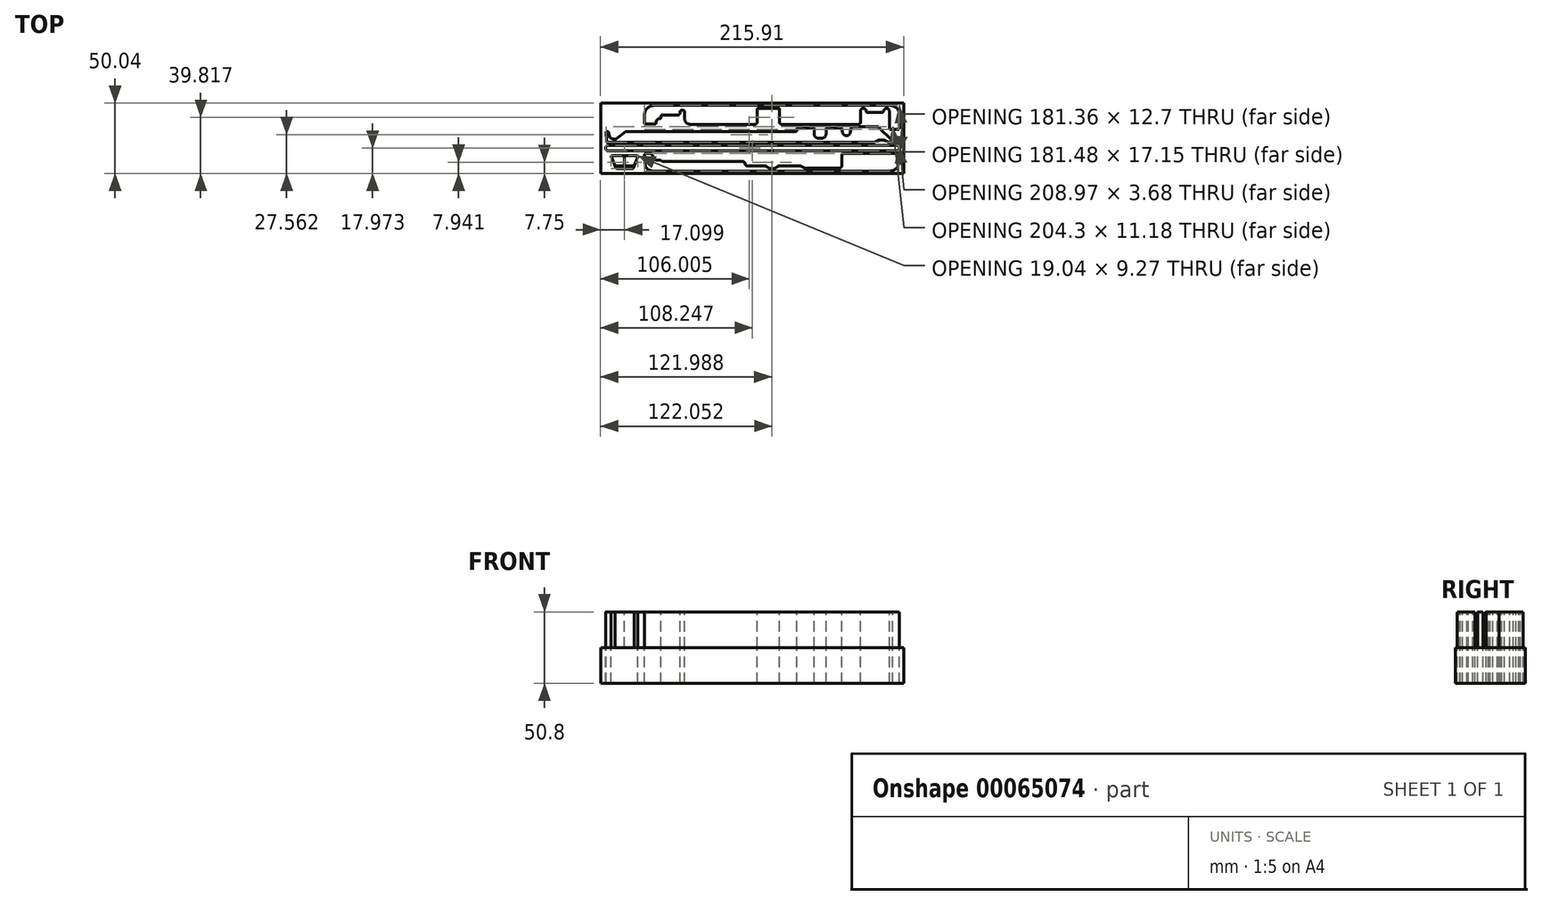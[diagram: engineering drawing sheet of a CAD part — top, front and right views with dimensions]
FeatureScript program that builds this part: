
annotation { "Feature Type Name" : "Feature", "Feature Type Description" : "" }
export const myFeature = defineFeature(function(context is Context, id is Id, definition is map)
    precondition{}
    {
        {
            var Q0;
            Q0=qCreatedBy(makeId("Top.planeOp"),FACE);
            var sketch = newSketch(context, id + "F0", { "sketchPlane" : qUnion([Q0])});
            skLineSegment(sketch, "E0", {"start": v(-180.88, 0) * mm, "end": v(0, 0) * mm});
            skLineSegment(sketch, "E1", {"start": v(0, 0) * mm, "end": v(0, 11.43) * mm});
            skLineSegment(sketch, "E2", {"start": v(-1.27, 12.7) * mm, "end": v(-39.67, 12.7) * mm});
            skLineSegment(sketch, "E3", {"start": v(-40.94, 11.43) * mm, "end": v(-40.94, 3.63) * mm});
            skLineSegment(sketch, "E4", {"start": v(-42.21, 2.36) * mm, "end": v(-67.28, 2.36) * mm});
            skLineSegment(sketch, "E5", {"start": v(-67.82, 2.48) * mm, "end": v(-70.48, 3.74) * mm});
            skLineSegment(sketch, "E6", {"start": v(-71.02, 3.86) * mm, "end": v(-85.51, 3.86) * mm});
            skLineSegment(sketch, "E7", {"start": v(-86.15, 3.7) * mm, "end": v(-88.59, 2.29) * mm});
            skLineSegment(sketch, "E8", {"start": v(-92.39, 2.29) * mm, "end": v(-94.83, 3.7) * mm});
            skLineSegment(sketch, "E9", {"start": v(-95.46, 3.86) * mm, "end": v(-108.29, 3.86) * mm});
            skLineSegment(sketch, "E10", {"start": v(-109.47, 4.65) * mm, "end": v(-110.1, 6.2) * mm});
            skLineSegment(sketch, "E11", {"start": v(-111.27, 6.98) * mm, "end": v(-168.18, 6.98) * mm});
            skLineSegment(sketch, "E12", {"start": v(-168.8, 7.15) * mm, "end": v(-170.13, 7.9) * mm});
            skLineSegment(sketch, "E13", {"start": v(-170.76, 8.08) * mm, "end": v(-173.2, 8.08) * mm});
            skLineSegment(sketch, "E14", {"start": v(-174.38, 8.9) * mm, "end": v(-174.9, 10.28) * mm});
            skLineSegment(sketch, "E15", {"start": v(-175.06, 10.53) * mm, "end": v(-176.6, 12.38) * mm});
            skLineSegment(sketch, "E16", {"start": v(-177.28, 12.7) * mm, "end": v(-180.47, 12.7) * mm});
            skLineSegment(sketch, "E17", {"start": v(-181.36, 11.78) * mm, "end": v(-180.88, 0) * mm});
            skFitSpline(sketch, "E18", {"points": [v(-181.13, 6.1) * mm, v(-172.76, 0) * mm], "startDerivative": vector(0.46, -11.6) * mm, "endDerivative": vector(18.6, 0) * mm});
            skFitSpline(sketch, "E19", {"points": [v(0, 6.73) * mm, v(-7.37, 0) * mm], "startDerivative": vector(0, -6.53) * mm, "endDerivative": vector(-15.85, 0) * mm});
            skPoint(sketch, "E20.visualSharp", {"position": v(0, 12.7) * mm});
            skArc(sketch, "E20.filletArc", {"start": v(0, 11.43) * mm, "mid": v(-0.37, 12.33) * mm, "end": v(-1.27, 12.7) * mm});
            skPoint(sketch, "E21.visualSharp", {"position": v(-40.94, 12.7) * mm});
            skArc(sketch, "E21.filletArc", {"start": v(-39.67, 12.7) * mm, "mid": v(-40.57, 12.33) * mm, "end": v(-40.94, 11.43) * mm});
            skPoint(sketch, "E22.visualSharp", {"position": v(-40.94, 2.36) * mm});
            skArc(sketch, "E22.filletArc", {"start": v(-42.21, 2.36) * mm, "mid": v(-41.32, 2.73) * mm, "end": v(-40.94, 3.63) * mm});
            skPoint(sketch, "E23.visualSharp", {"position": v(-67.56, 2.36) * mm});
            skArc(sketch, "E23.filletArc", {"start": v(-67.82, 2.48) * mm, "mid": v(-67.56, 2.4) * mm, "end": v(-67.28, 2.36) * mm});
            skPoint(sketch, "E24.visualSharp", {"position": v(-70.74, 3.86) * mm});
            skArc(sketch, "E24.filletArc", {"start": v(-70.48, 3.74) * mm, "mid": v(-70.75, 3.83) * mm, "end": v(-71.02, 3.86) * mm});
            skPoint(sketch, "E25.visualSharp", {"position": v(-85.85, 3.86) * mm});
            skArc(sketch, "E25.filletArc", {"start": v(-85.51, 3.86) * mm, "mid": v(-85.84, 3.82) * mm, "end": v(-86.15, 3.7) * mm});
            skPoint(sketch, "E26.visualSharp", {"position": v(-95.12, 3.86) * mm});
            skArc(sketch, "E26.filletArc", {"start": v(-94.83, 3.7) * mm, "mid": v(-95.13, 3.82) * mm, "end": v(-95.46, 3.86) * mm});
            skPoint(sketch, "E27.visualSharp", {"position": v(-109.14, 3.86) * mm});
            skArc(sketch, "E27.filletArc", {"start": v(-109.47, 4.65) * mm, "mid": v(-109, 4.08) * mm, "end": v(-108.29, 3.86) * mm});
            skPoint(sketch, "E28.visualSharp", {"position": v(-110.41, 6.98) * mm});
            skArc(sketch, "E28.filletArc", {"start": v(-110.1, 6.2) * mm, "mid": v(-110.56, 6.77) * mm, "end": v(-111.27, 6.99) * mm});
            skPoint(sketch, "E29.visualSharp", {"position": v(-168.51, 6.98) * mm});
            skArc(sketch, "E29.filletArc", {"start": v(-168.8, 7.15) * mm, "mid": v(-168.5, 7.03) * mm, "end": v(-168.18, 6.98) * mm});
            skPoint(sketch, "E30.visualSharp", {"position": v(-170.42, 8.08) * mm});
            skArc(sketch, "E30.filletArc", {"start": v(-170.13, 7.9) * mm, "mid": v(-170.43, 8.03) * mm, "end": v(-170.76, 8.08) * mm});
            skPoint(sketch, "E31.visualSharp", {"position": v(-174.07, 8.08) * mm});
            skArc(sketch, "E31.filletArc", {"start": v(-174.38, 8.9) * mm, "mid": v(-173.92, 8.3) * mm, "end": v(-173.2, 8.08) * mm});
            skPoint(sketch, "E32.visualSharp", {"position": v(-181.4, 12.7) * mm});
            skArc(sketch, "E32.filletArc", {"start": v(-180.47, 12.7) * mm, "mid": v(-181.1, 12.43) * mm, "end": v(-181.36, 11.78) * mm});
            skPoint(sketch, "E33.visualSharp", {"position": v(-176.87, 12.7) * mm});
            skArc(sketch, "E33.filletArc", {"start": v(-176.6, 12.38) * mm, "mid": v(-176.9, 12.62) * mm, "end": v(-177.28, 12.7) * mm});
            skPoint(sketch, "E34.visualSharp", {"position": v(-174.96, 10.41) * mm});
            skArc(sketch, "E34.filletArc", {"start": v(-174.9, 10.28) * mm, "mid": v(-174.97, 10.4) * mm, "end": v(-175.06, 10.53) * mm});
            skPoint(sketch, "E35.visualSharp", {"position": v(-90.49, 1.2) * mm});
            skArc(sketch, "E35.filletArc", {"start": v(-92.39, 2.29) * mm, "mid": v(-90.49, 1.78) * mm, "end": v(-88.59, 2.29) * mm});
            skLineSegment(sketch, "E36.bottom", {"start": v(-207.7, 18.41) * mm, "end": v(-1.27, 18.41) * mm});
            skLineSegment(sketch, "E36.top", {"start": v(-207.7, 14.73) * mm, "end": v(-1.27, 14.73) * mm});
            skLineSegment(sketch, "E36.left", {"start": v(-208.97, 17.14) * mm, "end": v(-208.97, 16) * mm});
            skLineSegment(sketch, "E36.right", {"start": v(0, 17.14) * mm, "end": v(0, 16) * mm});
            skPoint(sketch, "E37.visualSharp", {"position": v(-208.97, 18.41) * mm});
            skArc(sketch, "E37.filletArc", {"start": v(-207.7, 18.41) * mm, "mid": v(-208.6, 18.04) * mm, "end": v(-208.97, 17.14) * mm});
            skPoint(sketch, "E38.visualSharp", {"position": v(-208.97, 14.73) * mm});
            skArc(sketch, "E38.filletArc", {"start": v(-208.97, 16) * mm, "mid": v(-208.6, 15.1) * mm, "end": v(-207.7, 14.73) * mm});
            skPoint(sketch, "E39.visualSharp", {"position": v(0, 18.41) * mm});
            skArc(sketch, "E39.filletArc", {"start": v(0, 17.14) * mm, "mid": v(-0.37, 18.04) * mm, "end": v(-1.27, 18.41) * mm});
            skPoint(sketch, "E40.visualSharp", {"position": v(0, 14.73) * mm});
            skArc(sketch, "E40.filletArc", {"start": v(-1.27, 14.73) * mm, "mid": v(-0.37, 15.1) * mm, "end": v(0, 16) * mm});
            skLineSegment(sketch, "E41", {"start": v(-204.4, 11.18) * mm, "end": v(-186.87, 11.18) * mm});
            skLineSegment(sketch, "E42", {"start": v(-186.17, 10.12) * mm, "end": v(-189.46, 2.37) * mm});
            skLineSegment(sketch, "E43", {"start": v(-190.17, 1.9) * mm, "end": v(-201.1, 1.9) * mm});
            skLineSegment(sketch, "E44", {"start": v(-201.8, 2.37) * mm, "end": v(-205.1, 10.12) * mm});
            skPoint(sketch, "E45.visualSharp", {"position": v(-205.55, 11.18) * mm});
            skArc(sketch, "E45.filletArc", {"start": v(-204.4, 11.18) * mm, "mid": v(-205.03, 10.83) * mm, "end": v(-205.1, 10.12) * mm});
            skPoint(sketch, "E46.visualSharp", {"position": v(-185.72, 11.18) * mm});
            skArc(sketch, "E46.filletArc", {"start": v(-186.17, 10.12) * mm, "mid": v(-186.23, 10.83) * mm, "end": v(-186.87, 11.18) * mm});
            skPoint(sketch, "E47.visualSharp", {"position": v(-189.66, 1.9) * mm});
            skArc(sketch, "E47.filletArc", {"start": v(-190.17, 1.9) * mm, "mid": v(-189.75, 2.03) * mm, "end": v(-189.46, 2.37) * mm});
            skPoint(sketch, "E48.visualSharp", {"position": v(-201.6, 1.9) * mm});
            skArc(sketch, "E48.filletArc", {"start": v(-201.8, 2.37) * mm, "mid": v(-201.52, 2.03) * mm, "end": v(-201.1, 1.9) * mm});
            skLineSegment(sketch, "E49", {"start": v(-202.46, 3.94) * mm, "end": v(-188.8, 3.94) * mm});
            skLineSegment(sketch, "E50", {"start": v(-195.63, 3.94) * mm, "end": v(-195.63, 11.18) * mm});
            skLineSegment(sketch, "E51", {"start": v(-207.8, 20.57) * mm, "end": v(-17.9, 20.57) * mm});
            skArc(sketch, "E52", {"start": v(-7.43, 20.72) * mm, "mid": v(-12.45, 22.35) * mm, "end": v(-17.46, 20.72) * mm});
            skLineSegment(sketch, "E53", {"start": v(-6.98, 20.57) * mm, "end": v(-5.33, 20.57) * mm});
            skLineSegment(sketch, "E54", {"start": v(-4.8, 21.88) * mm, "end": v(-14.64, 31.53) * mm});
            skLineSegment(sketch, "E55", {"start": v(-15.17, 31.75) * mm, "end": v(-33.5, 31.75) * mm});
            skLineSegment(sketch, "E56", {"start": v(-34.25, 31.09) * mm, "end": v(-34.66, 27.91) * mm});
            skArc(sketch, "E57", {"start": v(-40.37, 27.91) * mm, "mid": v(-37.51, 25.4) * mm, "end": v(-34.66, 27.91) * mm});
            skLineSegment(sketch, "E58", {"start": v(-40.37, 27.91) * mm, "end": v(-40.68, 30.32) * mm});
            skLineSegment(sketch, "E59", {"start": v(-41.44, 30.99) * mm, "end": v(-51.3, 30.99) * mm});
            skLineSegment(sketch, "E60", {"start": v(-52.07, 30.23) * mm, "end": v(-52.07, 26.42) * mm});
            skLineSegment(sketch, "E61", {"start": v(-54.86, 23.62) * mm, "end": v(-57.66, 23.62) * mm});
            skLineSegment(sketch, "E62", {"start": v(-60.45, 26.42) * mm, "end": v(-60.45, 30.23) * mm});
            skLineSegment(sketch, "E63", {"start": v(-61.21, 30.99) * mm, "end": v(-72, 30.99) * mm});
            skLineSegment(sketch, "E64", {"start": v(-72.77, 30.23) * mm, "end": v(-72.77, 29.21) * mm});
            skLineSegment(sketch, "E65", {"start": v(-73.53, 28.45) * mm, "end": v(-194.3, 28.45) * mm});
            skLineSegment(sketch, "E66", {"start": v(-194.77, 28.29) * mm, "end": v(-201.34, 23.15) * mm});
            skLineSegment(sketch, "E67", {"start": v(-201.81, 22.99) * mm, "end": v(-203.32, 22.99) * mm});
            skLineSegment(sketch, "E68", {"start": v(-203.58, 23.03) * mm, "end": v(-205.86, 23.86) * mm});
            skLineSegment(sketch, "E69", {"start": v(-206.34, 24.4) * mm, "end": v(-207.13, 27.86) * mm});
            skLineSegment(sketch, "E70", {"start": v(-207.87, 28.45) * mm, "end": v(-208.11, 28.45) * mm});
            skLineSegment(sketch, "E71", {"start": v(-208.87, 27.65) * mm, "end": v(-208.57, 21.3) * mm});
            skPoint(sketch, "E72.visualSharp", {"position": v(-3.47, 20.57) * mm});
            skArc(sketch, "E72.filletArc", {"start": v(-5.33, 20.57) * mm, "mid": v(-4.63, 21.05) * mm, "end": v(-4.8, 21.88) * mm});
            skPoint(sketch, "E73.visualSharp", {"position": v(-14.86, 31.75) * mm});
            skArc(sketch, "E73.filletArc", {"start": v(-14.64, 31.53) * mm, "mid": v(-14.88, 31.7) * mm, "end": v(-15.17, 31.75) * mm});
            skPoint(sketch, "E74.visualSharp", {"position": v(-34.16, 31.75) * mm});
            skArc(sketch, "E74.filletArc", {"start": v(-33.5, 31.75) * mm, "mid": v(-34, 31.56) * mm, "end": v(-34.25, 31.09) * mm});
            skPoint(sketch, "E75.visualSharp", {"position": v(-40.77, 30.99) * mm});
            skArc(sketch, "E75.filletArc", {"start": v(-40.68, 30.32) * mm, "mid": v(-40.93, 30.8) * mm, "end": v(-41.44, 30.99) * mm});
            skPoint(sketch, "E76.visualSharp", {"position": v(-52.07, 30.99) * mm});
            skArc(sketch, "E76.filletArc", {"start": v(-51.3, 30.99) * mm, "mid": v(-51.85, 30.76) * mm, "end": v(-52.07, 30.23) * mm});
            skPoint(sketch, "E77.visualSharp", {"position": v(-60.45, 30.99) * mm});
            skArc(sketch, "E77.filletArc", {"start": v(-60.45, 30.23) * mm, "mid": v(-60.68, 30.76) * mm, "end": v(-61.21, 30.99) * mm});
            skPoint(sketch, "E78.visualSharp", {"position": v(-72.77, 30.99) * mm});
            skArc(sketch, "E78.filletArc", {"start": v(-72, 30.99) * mm, "mid": v(-72.55, 30.76) * mm, "end": v(-72.77, 30.23) * mm});
            skPoint(sketch, "E79.visualSharp", {"position": v(-72.77, 28.45) * mm});
            skArc(sketch, "E79.filletArc", {"start": v(-73.53, 28.45) * mm, "mid": v(-73, 28.67) * mm, "end": v(-72.77, 29.21) * mm});
            skPoint(sketch, "E80.visualSharp", {"position": v(-194.56, 28.45) * mm});
            skArc(sketch, "E80.filletArc", {"start": v(-194.3, 28.45) * mm, "mid": v(-194.55, 28.4) * mm, "end": v(-194.77, 28.29) * mm});
            skPoint(sketch, "E81.visualSharp", {"position": v(-201.55, 22.99) * mm});
            skArc(sketch, "E81.filletArc", {"start": v(-201.81, 22.99) * mm, "mid": v(-201.56, 23.03) * mm, "end": v(-201.34, 23.15) * mm});
            skPoint(sketch, "E82.visualSharp", {"position": v(-203.45, 22.99) * mm});
            skArc(sketch, "E82.filletArc", {"start": v(-203.58, 23.03) * mm, "mid": v(-203.45, 23) * mm, "end": v(-203.32, 22.99) * mm});
            skPoint(sketch, "E83.visualSharp", {"position": v(-206.25, 24) * mm});
            skArc(sketch, "E83.filletArc", {"start": v(-206.34, 24.4) * mm, "mid": v(-206.17, 24.07) * mm, "end": v(-205.86, 23.86) * mm});
            skPoint(sketch, "E84.visualSharp", {"position": v(-207.26, 28.45) * mm});
            skArc(sketch, "E84.filletArc", {"start": v(-207.13, 27.86) * mm, "mid": v(-207.4, 28.28) * mm, "end": v(-207.87, 28.45) * mm});
            skPoint(sketch, "E85.visualSharp", {"position": v(-208.91, 28.45) * mm});
            skArc(sketch, "E85.filletArc", {"start": v(-208.11, 28.45) * mm, "mid": v(-208.67, 28.21) * mm, "end": v(-208.87, 27.65) * mm});
            skPoint(sketch, "E86.visualSharp", {"position": v(-208.53, 20.57) * mm});
            skArc(sketch, "E86.filletArc", {"start": v(-208.57, 21.3) * mm, "mid": v(-208.33, 20.78) * mm, "end": v(-207.8, 20.57) * mm});
            skPoint(sketch, "E87.visualSharp", {"position": v(-52.07, 23.62) * mm});
            skArc(sketch, "E87.filletArc", {"start": v(-54.86, 23.62) * mm, "mid": v(-52.89, 24.44) * mm, "end": v(-52.07, 26.42) * mm});
            skPoint(sketch, "E88.visualSharp", {"position": v(-60.45, 23.62) * mm});
            skArc(sketch, "E88.filletArc", {"start": v(-60.45, 26.42) * mm, "mid": v(-59.63, 24.44) * mm, "end": v(-57.66, 23.62) * mm});
            skLineSegment(sketch, "E89", {"start": v(-14.86, 31.75) * mm, "end": v(-4.57, 31.75) * mm, "construction": true});
            skLineSegment(sketch, "E90", {"start": v(-4.57, 31.75) * mm, "end": v(-4.57, 21.34) * mm, "construction": true});
            skPoint(sketch, "E91.visualSharp", {"position": v(-17.65, 20.57) * mm});
            skArc(sketch, "E91.filletArc", {"start": v(-17.9, 20.57) * mm, "mid": v(-17.67, 20.61) * mm, "end": v(-17.46, 20.72) * mm});
            skPoint(sketch, "E92.visualSharp", {"position": v(-7.24, 20.57) * mm});
            skArc(sketch, "E92.filletArc", {"start": v(-7.43, 20.72) * mm, "mid": v(-7.22, 20.61) * mm, "end": v(-6.98, 20.57) * mm});
            skLineSegment(sketch, "E93", {"start": v(-181.48, 47) * mm, "end": v(-181.48, 34.42) * mm});
            skLineSegment(sketch, "E94", {"start": v(-180.72, 33.66) * mm, "end": v(-173.92, 33.66) * mm});
            skLineSegment(sketch, "E95", {"start": v(-173.16, 34.34) * mm, "end": v(-173.07, 35.3) * mm});
            skLineSegment(sketch, "E96", {"start": v(-170.54, 37.6) * mm, "end": v(-170.43, 37.6) * mm});
            skLineSegment(sketch, "E97", {"start": v(-169.67, 38.35) * mm, "end": v(-169.67, 39.37) * mm});
            skLineSegment(sketch, "E98", {"start": v(-168.9, 40.13) * mm, "end": v(-157.6, 40.13) * mm});
            skLineSegment(sketch, "E99", {"start": v(-156.08, 41.66) * mm, "end": v(-156.08, 42.16) * mm});
            skLineSegment(sketch, "E100", {"start": v(-154.56, 43.69) * mm, "end": v(-154.3, 43.69) * mm});
            skLineSegment(sketch, "E101", {"start": v(-152.78, 42.16) * mm, "end": v(-152.78, 37.34) * mm});
            skLineSegment(sketch, "E102", {"start": v(-148.97, 33.53) * mm, "end": v(-102.62, 33.53) * mm});
            skLineSegment(sketch, "E103", {"start": v(-101.1, 35.05) * mm, "end": v(-101.1, 44.2) * mm});
            skLineSegment(sketch, "E104", {"start": v(-100.33, 44.96) * mm, "end": v(-85.98, 44.96) * mm});
            skLineSegment(sketch, "E105", {"start": v(-85.22, 44.2) * mm, "end": v(-85.22, 35.05) * mm});
            skLineSegment(sketch, "E106", {"start": v(-83.7, 33.53) * mm, "end": v(-28.96, 33.53) * mm});
            skLineSegment(sketch, "E107", {"start": v(-27.43, 35.05) * mm, "end": v(-27.43, 43.05) * mm});
            skArc(sketch, "E108", {"start": v(-23.76, 43.78) * mm, "mid": v(-25.9, 44.92) * mm, "end": v(-27.43, 43.05) * mm});
            skLineSegment(sketch, "E109", {"start": v(-23.76, 43.78) * mm, "end": v(-23.24, 42.5) * mm});
            skLineSegment(sketch, "E110", {"start": v(-22.54, 42.04) * mm, "end": v(-11.88, 42.04) * mm});
            skLineSegment(sketch, "E111", {"start": v(-11.17, 42.5) * mm, "end": v(-10.65, 43.78) * mm});
            skArc(sketch, "E112", {"start": v(-6.98, 43.05) * mm, "mid": v(-8.52, 44.92) * mm, "end": v(-10.65, 43.78) * mm});
            skLineSegment(sketch, "E113", {"start": v(-6.98, 43.05) * mm, "end": v(-6.98, 30.6) * mm});
            skLineSegment(sketch, "E114", {"start": v(-6.22, 29.84) * mm, "end": v(-0.76, 29.84) * mm});
            skLineSegment(sketch, "E115", {"start": v(0, 30.6) * mm, "end": v(0, 47) * mm});
            skLineSegment(sketch, "E116", {"start": v(0, 47) * mm, "end": v(-181.48, 47) * mm});
            skPoint(sketch, "E117.visualSharp", {"position": v(-23.05, 42.04) * mm});
            skArc(sketch, "E117.filletArc", {"start": v(-23.24, 42.5) * mm, "mid": v(-22.96, 42.17) * mm, "end": v(-22.54, 42.04) * mm});
            skPoint(sketch, "E118.visualSharp", {"position": v(-11.37, 42.04) * mm});
            skArc(sketch, "E118.filletArc", {"start": v(-11.88, 42.04) * mm, "mid": v(-11.45, 42.17) * mm, "end": v(-11.17, 42.5) * mm});
            skPoint(sketch, "E119.visualSharp", {"position": v(-6.98, 29.84) * mm});
            skArc(sketch, "E119.filletArc", {"start": v(-6.98, 30.6) * mm, "mid": v(-6.76, 30.07) * mm, "end": v(-6.22, 29.84) * mm});
            skPoint(sketch, "E120.visualSharp", {"position": v(0, 29.84) * mm});
            skArc(sketch, "E120.filletArc", {"start": v(-0.76, 29.84) * mm, "mid": v(-0.22, 30.07) * mm, "end": v(0, 30.6) * mm});
            skPoint(sketch, "E121.visualSharp", {"position": v(-101.1, 44.96) * mm});
            skArc(sketch, "E121.filletArc", {"start": v(-100.33, 44.96) * mm, "mid": v(-100.87, 44.73) * mm, "end": v(-101.1, 44.2) * mm});
            skPoint(sketch, "E122.visualSharp", {"position": v(-85.22, 44.96) * mm});
            skArc(sketch, "E122.filletArc", {"start": v(-85.22, 44.2) * mm, "mid": v(-85.44, 44.73) * mm, "end": v(-85.98, 44.96) * mm});
            skPoint(sketch, "E123.visualSharp", {"position": v(-169.67, 37.6) * mm});
            skArc(sketch, "E123.filletArc", {"start": v(-170.43, 37.6) * mm, "mid": v(-169.9, 37.82) * mm, "end": v(-169.67, 38.35) * mm});
            skPoint(sketch, "E124.visualSharp", {"position": v(-169.67, 40.13) * mm});
            skArc(sketch, "E124.filletArc", {"start": v(-168.9, 40.13) * mm, "mid": v(-169.45, 39.9) * mm, "end": v(-169.67, 39.37) * mm});
            skPoint(sketch, "E125.visualSharp", {"position": v(-181.48, 33.66) * mm});
            skArc(sketch, "E125.filletArc", {"start": v(-181.48, 34.42) * mm, "mid": v(-181.26, 33.88) * mm, "end": v(-180.72, 33.66) * mm});
            skPoint(sketch, "E126.visualSharp", {"position": v(-173.23, 33.66) * mm});
            skArc(sketch, "E126.filletArc", {"start": v(-173.92, 33.65) * mm, "mid": v(-173.4, 33.85) * mm, "end": v(-173.16, 34.34) * mm});
            skPoint(sketch, "E127.visualSharp", {"position": v(-101.1, 33.53) * mm});
            skArc(sketch, "E127.filletArc", {"start": v(-102.62, 33.53) * mm, "mid": v(-101.54, 33.97) * mm, "end": v(-101.1, 35.05) * mm});
            skPoint(sketch, "E128.visualSharp", {"position": v(-85.22, 33.53) * mm});
            skArc(sketch, "E128.filletArc", {"start": v(-85.22, 35.05) * mm, "mid": v(-84.77, 33.97) * mm, "end": v(-83.7, 33.53) * mm});
            skPoint(sketch, "E129.visualSharp", {"position": v(-27.43, 33.53) * mm});
            skArc(sketch, "E129.filletArc", {"start": v(-28.96, 33.53) * mm, "mid": v(-27.88, 33.97) * mm, "end": v(-27.43, 35.05) * mm});
            skPoint(sketch, "E130.visualSharp", {"position": v(-156.08, 40.13) * mm});
            skArc(sketch, "E130.filletArc", {"start": v(-157.6, 40.13) * mm, "mid": v(-156.53, 40.58) * mm, "end": v(-156.08, 41.66) * mm});
            skPoint(sketch, "E131.visualSharp", {"position": v(-156.08, 43.69) * mm});
            skArc(sketch, "E131.filletArc", {"start": v(-154.56, 43.69) * mm, "mid": v(-155.64, 43.24) * mm, "end": v(-156.08, 42.16) * mm});
            skPoint(sketch, "E132.visualSharp", {"position": v(-152.78, 43.69) * mm});
            skArc(sketch, "E132.filletArc", {"start": v(-152.78, 42.16) * mm, "mid": v(-153.23, 43.24) * mm, "end": v(-154.3, 43.69) * mm});
            skPoint(sketch, "E133.visualSharp", {"position": v(-172.85, 37.6) * mm});
            skArc(sketch, "E133.filletArc", {"start": v(-170.54, 37.6) * mm, "mid": v(-172.25, 36.93) * mm, "end": v(-173.07, 35.3) * mm});
            skPoint(sketch, "E134.visualSharp", {"position": v(-152.78, 33.53) * mm});
            skArc(sketch, "E134.filletArc", {"start": v(-152.78, 37.34) * mm, "mid": v(-151.67, 34.64) * mm, "end": v(-148.97, 33.53) * mm});
            skLineSegment(sketch, "E135", {"start": v(-72.77, 28.45) * mm, "end": v(-72, 28.45) * mm, "construction": true});
            skLineSegment(sketch, "E136", {"start": v(-72, 28.45) * mm, "end": v(-61.21, 28.45) * mm});
            skLineSegment(sketch, "E137", {"start": v(-61.21, 28.45) * mm, "end": v(-60.45, 28.45) * mm, "construction": true});
            skLineSegment(sketch, "E138", {"start": v(-60.45, 28.45) * mm, "end": v(-52.07, 28.45) * mm, "construction": true});
            skLineSegment(sketch, "E139", {"start": v(-52.07, 28.45) * mm, "end": v(-51.34, 28.45) * mm, "construction": true});
            skLineSegment(sketch, "E140", {"start": v(-51.34, 28.45) * mm, "end": v(-41.18, 28.45) * mm});
            skLineSegment(sketch, "E141", {"start": v(-41.18, 28.45) * mm, "end": v(-40.44, 28.45) * mm, "construction": true});
            skLineSegment(sketch, "E142", {"start": v(-40.44, 28.45) * mm, "end": v(-34.59, 28.45) * mm, "construction": true});
            skLineSegment(sketch, "E143", {"start": v(-34.59, 28.45) * mm, "end": v(-33.52, 28.45) * mm, "construction": true});
            skLineSegment(sketch, "E144", {"start": v(-33.52, 28.45) * mm, "end": v(-12.56, 28.45) * mm});
            skLineSegment(sketch, "E145", {"start": v(-12.56, 28.45) * mm, "end": v(-11.5, 28.45) * mm, "construction": true});
            skFitSpline(sketch, "E146", {"points": [v(-181.48, 39.12) * mm, v(-173.6, 47) * mm], "startDerivative": vector(0, 16.61) * mm, "endDerivative": vector(14.86, 0) * mm});
            skFitSpline(sketch, "E147", {"points": [v(-7.37, 47) * mm, v(0, 40.26) * mm], "startDerivative": vector(17.08, 0) * mm, "endDerivative": vector(0, -10.36) * mm});
            skLineSegment(sketch, "E148.bottom", {"start": v(-212.72, 48.64) * mm, "end": v(3.17, 48.64) * mm});
            skLineSegment(sketch, "E148.top", {"start": v(-212.72, -1.4) * mm, "end": v(3.17, -1.4) * mm});
            skLineSegment(sketch, "E148.left", {"start": v(-212.72, 48.64) * mm, "end": v(-212.72, -1.4) * mm});
            skLineSegment(sketch, "E148.right", {"start": v(3.17, 48.64) * mm, "end": v(3.18, -1.4) * mm});
            skSolve(sketch);
        }
        {
            var Q0;
            Q0=makeQuery(id+"F0.imprint","IMPRINT",FACE,{"disambiguationData":[TD([[makeQuery(id+"F0.imprint","IMPRINT",EDGE,{"derivedFrom":sQuery(id+"F0.wireOp",EDGE,"E2")}),1.0]])]});
            var Q1;
            Q1=makeQuery(id+"F0.imprint","IMPRINT",FACE,{"disambiguationData":[TD([[makeQuery(id+"F0.imprint","IMPRINT",EDGE,{"derivedFrom":sQuery(id+"F0.wireOp",EDGE,"E36.bottom")}),-1.0]])]});
            var Q2;
            Q2=makeQuery(id+"F0.imprint","IMPRINT",FACE,{"disambiguationData":[TD([[makeQuery(id+"F0.imprint","IMPRINT",EDGE,{"derivedFrom":sQuery(id+"F0.wireOp",EDGE,"E51")}),1.0]])]});
            var Q3;
            Q3=makeQuery(id+"F0.imprint","IMPRINT",FACE,{"disambiguationData":[TD([[makeQuery(id+"F0.imprint","IMPRINT",EDGE,{"derivedFrom":sQuery(id+"F0.wireOp",EDGE,"E94")}),1.0]])]});
            var Q4;
            {var subQ4=sQuery(id+"F0.wireOp",EDGE,"E46.filletArc");Q4=makeQuery(id+"F0.imprint","IMPRINT",FACE,{"disambiguationData":[TD([[makeQuery(id+"F0.imprint","IMPRINT",EDGE,{"derivedFrom":subQ4}),1.0]])]});}
            extrude(context, id + "F1", {"entities" : qUnion([Q0, Q1, Q2, Q3, Q4]), "depth" : 25.4 * mm});
        }
        {
            var Q0;
            {var subQ4=sQuery(id+"F0.wireOp",EDGE,"E45.filletArc");Q0=makeQuery(id+"F0.imprint","IMPRINT",FACE,{"disambiguationData":[TD([[makeQuery(id+"F0.imprint","IMPRINT",EDGE,{"derivedFrom":subQ4}),1.0]])]});}
            extrude(context, id + "F2", {"entities" : qUnion([Q0]), "depth" : 25.4 * mm});
        }
        {
            var Q0;
            Q0=makeQuery(id+"F0.imprint","IMPRINT",FACE,{"disambiguationData":[TD([[makeQuery(id+"F0.imprint","IMPRINT",EDGE,{"derivedFrom":sQuery(id+"F0.wireOp",EDGE,"E43")}),-1.0]])]});
            extrude(context, id + "F3", {"entities" : qUnion([Q0]), "depth" : 25.4 * mm});
        }
        {
            var Q0;
            Q0=makeQuery(id+"F0.imprint","IMPRINT",FACE,{"disambiguationData":[TD([[makeQuery(id+"F0.imprint","IMPRINT",EDGE,{"derivedFrom":sQuery(id+"F0.wireOp",EDGE,"E2")}),-1.0]])]});
            var Q1;
            Q1=makeQuery(id+"F1.opExtrude","CAP_FACE",FACE,{"disambiguationData":[OSD([sQuery(id+"F0.wireOp",EDGE,"E93"),sQuery(id+"F0.wireOp",EDGE,"E94"),sQuery(id+"F0.wireOp",EDGE,"E95"),sQuery(id+"F0.wireOp",EDGE,"E96"),sQuery(id+"F0.wireOp",EDGE,"E97"),sQuery(id+"F0.wireOp",EDGE,"E98"),sQuery(id+"F0.wireOp",EDGE,"E99"),sQuery(id+"F0.wireOp",EDGE,"E100"),sQuery(id+"F0.wireOp",EDGE,"E101"),sQuery(id+"F0.wireOp",EDGE,"E102"),sQuery(id+"F0.wireOp",EDGE,"E103"),sQuery(id+"F0.wireOp",EDGE,"E104"),sQuery(id+"F0.wireOp",EDGE,"E105"),sQuery(id+"F0.wireOp",EDGE,"E106"),sQuery(id+"F0.wireOp",EDGE,"E107"),sQuery(id+"F0.wireOp",EDGE,"E108"),sQuery(id+"F0.wireOp",EDGE,"E109"),sQuery(id+"F0.wireOp",EDGE,"E110"),sQuery(id+"F0.wireOp",EDGE,"E111"),sQuery(id+"F0.wireOp",EDGE,"E112"),sQuery(id+"F0.wireOp",EDGE,"E113"),sQuery(id+"F0.wireOp",EDGE,"E114"),sQuery(id+"F0.wireOp",EDGE,"E115"),sQuery(id+"F0.wireOp",EDGE,"E116"),sQuery(id+"F0.wireOp",EDGE,"E117.filletArc"),sQuery(id+"F0.wireOp",EDGE,"E118.filletArc"),sQuery(id+"F0.wireOp",EDGE,"E119.filletArc"),sQuery(id+"F0.wireOp",EDGE,"E120.filletArc"),sQuery(id+"F0.wireOp",EDGE,"E121.filletArc"),sQuery(id+"F0.wireOp",EDGE,"E122.filletArc"),sQuery(id+"F0.wireOp",EDGE,"E123.filletArc"),sQuery(id+"F0.wireOp",EDGE,"E124.filletArc"),sQuery(id+"F0.wireOp",EDGE,"E125.filletArc"),sQuery(id+"F0.wireOp",EDGE,"E126.filletArc"),sQuery(id+"F0.wireOp",EDGE,"E127.filletArc"),sQuery(id+"F0.wireOp",EDGE,"E128.filletArc"),sQuery(id+"F0.wireOp",EDGE,"E129.filletArc"),sQuery(id+"F0.wireOp",EDGE,"E130.filletArc"),sQuery(id+"F0.wireOp",EDGE,"E131.filletArc"),sQuery(id+"F0.wireOp",EDGE,"E132.filletArc"),sQuery(id+"F0.wireOp",EDGE,"E133.filletArc"),sQuery(id+"F0.wireOp",EDGE,"E134.filletArc"),sQuery(id+"F0.wireOp",EDGE,"E146"),sQuery(id+"F0.wireOp",EDGE,"E147")])],"isStart":false});
            var Q2;
            {var subQ3=sQuery(id+"F0.wireOp",EDGE,"E146");Q2=makeQuery(id+"F0.imprint","IMPRINT",FACE,{"disambiguationData":[TD([[makeQuery(id+"F0.imprint","IMPRINT",EDGE,{"derivedFrom":subQ3}),1.0]])]});}
            var Q3;
            {var subQ3=sQuery(id+"F0.wireOp",EDGE,"E147");Q3=makeQuery(id+"F0.imprint","IMPRINT",FACE,{"disambiguationData":[TD([[makeQuery(id+"F0.imprint","IMPRINT",EDGE,{"derivedFrom":subQ3}),1.0]])]});}
            var Q4;
            Q4=makeQuery(id+"F1.opExtrude","CAP_FACE",FACE,{"disambiguationData":[OSD([sQuery(id+"F0.wireOp",EDGE,"E51"),sQuery(id+"F0.wireOp",EDGE,"E52"),sQuery(id+"F0.wireOp",EDGE,"E53"),sQuery(id+"F0.wireOp",EDGE,"E54"),sQuery(id+"F0.wireOp",EDGE,"E55"),sQuery(id+"F0.wireOp",EDGE,"E56"),sQuery(id+"F0.wireOp",EDGE,"E57"),sQuery(id+"F0.wireOp",EDGE,"E58"),sQuery(id+"F0.wireOp",EDGE,"E59"),sQuery(id+"F0.wireOp",EDGE,"E60"),sQuery(id+"F0.wireOp",EDGE,"E61"),sQuery(id+"F0.wireOp",EDGE,"E62"),sQuery(id+"F0.wireOp",EDGE,"E63"),sQuery(id+"F0.wireOp",EDGE,"E64"),sQuery(id+"F0.wireOp",EDGE,"E65"),sQuery(id+"F0.wireOp",EDGE,"E66"),sQuery(id+"F0.wireOp",EDGE,"E67"),sQuery(id+"F0.wireOp",EDGE,"E68"),sQuery(id+"F0.wireOp",EDGE,"E69"),sQuery(id+"F0.wireOp",EDGE,"E70"),sQuery(id+"F0.wireOp",EDGE,"E71"),sQuery(id+"F0.wireOp",EDGE,"E72.filletArc"),sQuery(id+"F0.wireOp",EDGE,"E73.filletArc"),sQuery(id+"F0.wireOp",EDGE,"E74.filletArc"),sQuery(id+"F0.wireOp",EDGE,"E75.filletArc"),sQuery(id+"F0.wireOp",EDGE,"E76.filletArc"),sQuery(id+"F0.wireOp",EDGE,"E77.filletArc"),sQuery(id+"F0.wireOp",EDGE,"E78.filletArc"),sQuery(id+"F0.wireOp",EDGE,"E79.filletArc"),sQuery(id+"F0.wireOp",EDGE,"E80.filletArc"),sQuery(id+"F0.wireOp",EDGE,"E81.filletArc"),sQuery(id+"F0.wireOp",EDGE,"E82.filletArc"),sQuery(id+"F0.wireOp",EDGE,"E83.filletArc"),sQuery(id+"F0.wireOp",EDGE,"E84.filletArc"),sQuery(id+"F0.wireOp",EDGE,"E85.filletArc"),sQuery(id+"F0.wireOp",EDGE,"E86.filletArc"),sQuery(id+"F0.wireOp",EDGE,"E87.filletArc"),sQuery(id+"F0.wireOp",EDGE,"E88.filletArc"),sQuery(id+"F0.wireOp",EDGE,"E91.filletArc"),sQuery(id+"F0.wireOp",EDGE,"E92.filletArc")])],"isStart":false});
            var Q5;
            Q5=makeQuery(id+"F1.opExtrude","CAP_FACE",FACE,{"disambiguationData":[OSD([sQuery(id+"F0.wireOp",EDGE,"E36.bottom"),sQuery(id+"F0.wireOp",EDGE,"E36.top"),sQuery(id+"F0.wireOp",EDGE,"E36.left"),sQuery(id+"F0.wireOp",EDGE,"E36.right"),sQuery(id+"F0.wireOp",EDGE,"E37.filletArc"),sQuery(id+"F0.wireOp",EDGE,"E38.filletArc"),sQuery(id+"F0.wireOp",EDGE,"E39.filletArc"),sQuery(id+"F0.wireOp",EDGE,"E40.filletArc")])],"isStart":false});
            var Q6;
            {var subQ3=sQuery(id+"F0.wireOp",EDGE,"E19");Q6=makeQuery(id+"F0.imprint","IMPRINT",FACE,{"disambiguationData":[TD([[makeQuery(id+"F0.imprint","IMPRINT",EDGE,{"derivedFrom":subQ3}),1.0]])]});}
            var Q7;
            Q7=makeQuery(id+"F1.opExtrude","CAP_FACE",FACE,{"disambiguationData":[OSD([sQuery(id+"F0.wireOp",EDGE,"E0"),sQuery(id+"F0.wireOp",EDGE,"E1"),sQuery(id+"F0.wireOp",EDGE,"E2"),sQuery(id+"F0.wireOp",EDGE,"E3"),sQuery(id+"F0.wireOp",EDGE,"E4"),sQuery(id+"F0.wireOp",EDGE,"E5"),sQuery(id+"F0.wireOp",EDGE,"E6"),sQuery(id+"F0.wireOp",EDGE,"E7"),sQuery(id+"F0.wireOp",EDGE,"E8"),sQuery(id+"F0.wireOp",EDGE,"E9"),sQuery(id+"F0.wireOp",EDGE,"E10"),sQuery(id+"F0.wireOp",EDGE,"E11"),sQuery(id+"F0.wireOp",EDGE,"E12"),sQuery(id+"F0.wireOp",EDGE,"E13"),sQuery(id+"F0.wireOp",EDGE,"E14"),sQuery(id+"F0.wireOp",EDGE,"E15"),sQuery(id+"F0.wireOp",EDGE,"E16"),sQuery(id+"F0.wireOp",EDGE,"E17"),sQuery(id+"F0.wireOp",EDGE,"E18"),sQuery(id+"F0.wireOp",EDGE,"E19"),sQuery(id+"F0.wireOp",EDGE,"E20.filletArc"),sQuery(id+"F0.wireOp",EDGE,"E21.filletArc"),sQuery(id+"F0.wireOp",EDGE,"E22.filletArc"),sQuery(id+"F0.wireOp",EDGE,"E23.filletArc"),sQuery(id+"F0.wireOp",EDGE,"E24.filletArc"),sQuery(id+"F0.wireOp",EDGE,"E25.filletArc"),sQuery(id+"F0.wireOp",EDGE,"E26.filletArc"),sQuery(id+"F0.wireOp",EDGE,"E27.filletArc"),sQuery(id+"F0.wireOp",EDGE,"E28.filletArc"),sQuery(id+"F0.wireOp",EDGE,"E29.filletArc"),sQuery(id+"F0.wireOp",EDGE,"E30.filletArc"),sQuery(id+"F0.wireOp",EDGE,"E31.filletArc"),sQuery(id+"F0.wireOp",EDGE,"E32.filletArc"),sQuery(id+"F0.wireOp",EDGE,"E33.filletArc"),sQuery(id+"F0.wireOp",EDGE,"E34.filletArc"),sQuery(id+"F0.wireOp",EDGE,"E35.filletArc")])],"isStart":false});
            var Q8;
            {var subQ3=sQuery(id+"F0.wireOp",EDGE,"E18");Q8=makeQuery(id+"F0.imprint","IMPRINT",FACE,{"disambiguationData":[TD([[makeQuery(id+"F0.imprint","IMPRINT",EDGE,{"derivedFrom":subQ3}),-1.0]])]});}
            var Q9;
            Q9=makeQuery(id+"F3.opExtrude","CAP_FACE",FACE,{"disambiguationData":[OSD([sQuery(id+"F0.wireOp",EDGE,"E42"),sQuery(id+"F0.wireOp",EDGE,"E43"),sQuery(id+"F0.wireOp",EDGE,"E44"),sQuery(id+"F0.wireOp",EDGE,"E47.filletArc"),sQuery(id+"F0.wireOp",EDGE,"E48.filletArc"),sQuery(id+"F0.wireOp",EDGE,"E49")])],"isStart":false});
            var Q10;
            Q10=makeQuery(id+"F1.opExtrude","CAP_FACE",FACE,{"disambiguationData":[OSD([sQuery(id+"F0.wireOp",EDGE,"E41"),sQuery(id+"F0.wireOp",EDGE,"E42"),sQuery(id+"F0.wireOp",EDGE,"E46.filletArc"),sQuery(id+"F0.wireOp",EDGE,"E49"),sQuery(id+"F0.wireOp",EDGE,"E50")])],"isStart":false});
            var Q11;
            Q11=makeQuery(id+"F2.opExtrude","CAP_FACE",FACE,{"disambiguationData":[OSD([sQuery(id+"F0.wireOp",EDGE,"E41"),sQuery(id+"F0.wireOp",EDGE,"E44"),sQuery(id+"F0.wireOp",EDGE,"E45.filletArc"),sQuery(id+"F0.wireOp",EDGE,"E49"),sQuery(id+"F0.wireOp",EDGE,"E50")])],"isStart":false});
            extrude(context, id + "F4", {"entities" : qUnion([Q0, Q1, Q2, Q3, Q4, Q5, Q6, Q7, Q8, Q9, Q10, Q11]), "oppositeDirection" : true, "depth" : 25.4 * mm});
        }
    });
